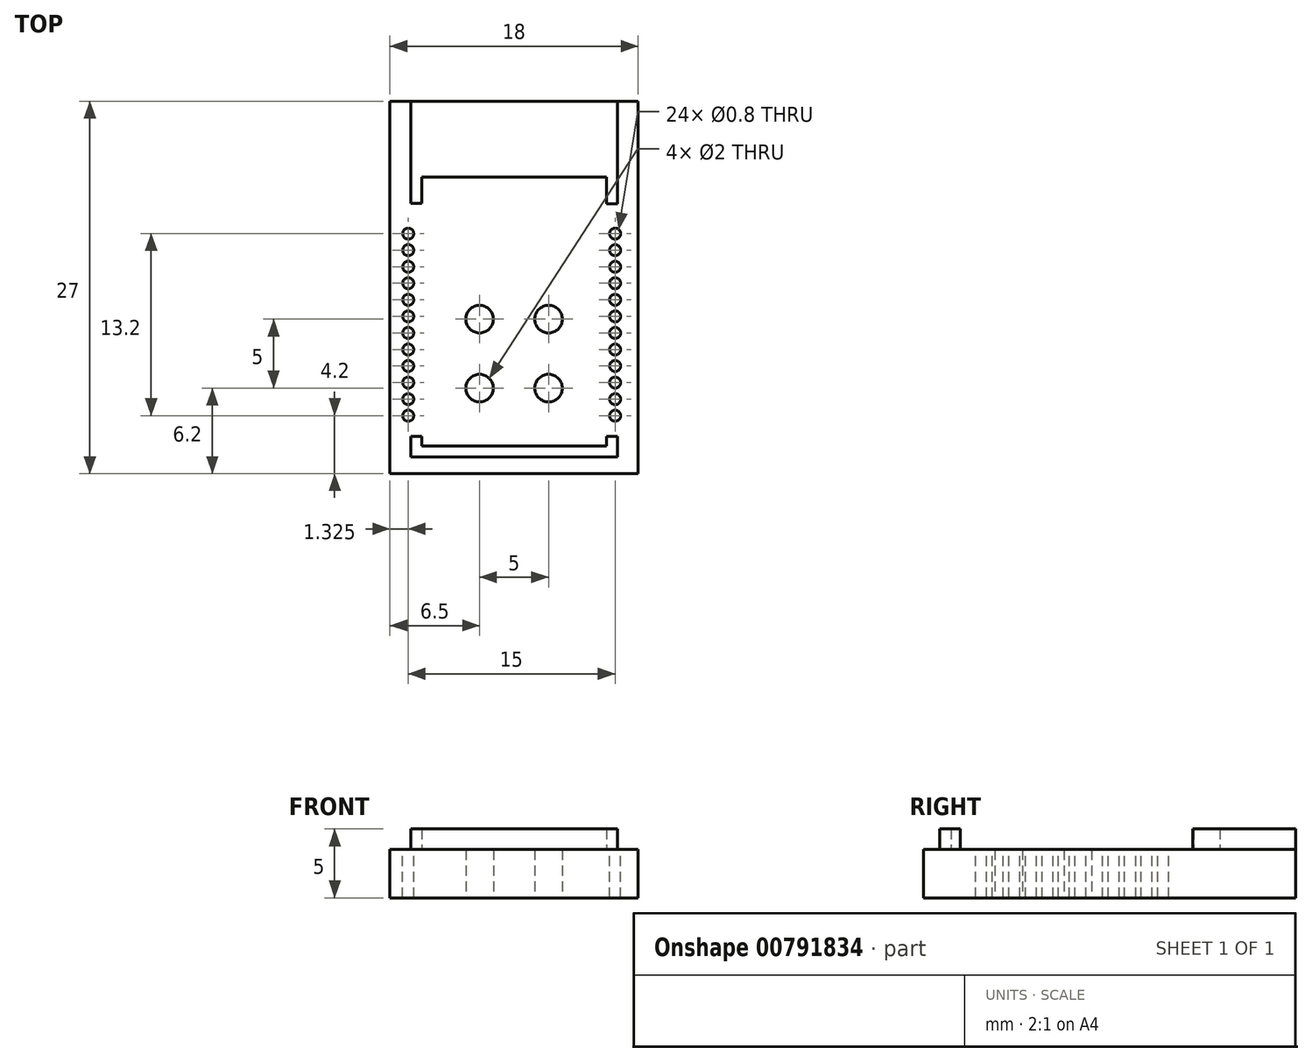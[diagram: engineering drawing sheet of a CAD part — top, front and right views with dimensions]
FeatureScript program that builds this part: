
annotation { "Feature Type Name" : "Feature", "Feature Type Description" : "" }
export const myFeature = defineFeature(function(context is Context, id is Id, definition is map)
    precondition{}
    {
        {
            var Q0;
            Q0=qCreatedBy(makeId("Top.planeOp"),FACE);
            var sketch = newSketch(context, id + "F0", { "sketchPlane" : qUnion([Q0])});
            skLineSegment(sketch, "E0.bottom", {"start": v(0, 0) * mm, "end": v(15, 0) * mm});
            skLineSegment(sketch, "E0.top", {"start": v(0, 25.8) * mm, "end": v(15, 25.8) * mm});
            skLineSegment(sketch, "E0.left", {"start": v(0, 0) * mm, "end": v(0, 1.49) * mm});
            skLineSegment(sketch, "E0.right", {"start": v(15, 0) * mm, "end": v(15, 1.49) * mm});
            skLineSegment(sketch, "E1.bottom", {"start": v(0.8, 0.8) * mm, "end": v(14.2, 0.8) * mm});
            skLineSegment(sketch, "E1.top", {"start": v(0.8, 20.3) * mm, "end": v(14.2, 20.3) * mm});
            skLineSegment(sketch, "E1.left", {"start": v(0.8, 0.8) * mm, "end": v(0.8, 1.49) * mm});
            skLineSegment(sketch, "E1.right", {"start": v(14.2, 0.8) * mm, "end": v(14.2, 1.49) * mm});
            skLineSegment(sketch, "E2.bottom", {"start": v(-1.5, -1.2) * mm, "end": v(16.5, -1.2) * mm});
            skLineSegment(sketch, "E2.top", {"start": v(-1.5, 25.8) * mm, "end": v(16.5, 25.8) * mm});
            skLineSegment(sketch, "E2.left", {"start": v(-1.5, -1.2) * mm, "end": v(-1.5, 25.8) * mm});
            skLineSegment(sketch, "E2.right", {"start": v(16.5, -1.2) * mm, "end": v(16.5, 25.8) * mm});
            skLineSegment(sketch, "E3.bottom", {"start": v(0, 1.49) * mm, "end": v(0.8, 1.49) * mm});
            skLineSegment(sketch, "E3.top", {"start": v(0, 18.4) * mm, "end": v(0.8, 18.4) * mm});
            skLineSegment(sketch, "E4.trimOffspring", {"start": v(0, 18.4) * mm, "end": v(0, 25.8) * mm});
            skLineSegment(sketch, "E5.trimOffspring", {"start": v(0.8, 18.4) * mm, "end": v(0.8, 20.3) * mm});
            skLineSegment(sketch, "E6.bottom", {"start": v(14.2, 1.49) * mm, "end": v(15, 1.49) * mm});
            skLineSegment(sketch, "E6.top", {"start": v(14.2, 18.35) * mm, "end": v(15, 18.35) * mm});
            skLineSegment(sketch, "E7.trimOffspring", {"start": v(14.2, 18.35) * mm, "end": v(14.2, 20.3) * mm});
            skLineSegment(sketch, "E8.trimOffspring", {"start": v(15, 18.35) * mm, "end": v(15, 25.8) * mm});
            skCircle(sketch, "E9", {"center": v(5, 5) * mm, "radius": 1 * mm});
            skCircle(sketch, "E10.0.1.0", {"center": v(5, 10) * mm, "radius": 1 * mm});
            skCircle(sketch, "E10.1.0.0", {"center": v(10, 5) * mm, "radius": 1 * mm});
            skCircle(sketch, "E10.1.1.0", {"center": v(10, 10) * mm, "radius": 1 * mm});
            skLineSegment(sketch, "E10.direction1", {"start": v(5, 5) * mm, "end": v(10, 5) * mm, "construction": true});
            skLineSegment(sketch, "E10.direction2", {"start": v(5, 5) * mm, "end": v(5, 10) * mm, "construction": true});
            skSolve(sketch);
        }
        {
            var Q0;
            Q0=makeQuery(id+"F0.imprint","IMPRINT",FACE,{"disambiguationData":[TD([[makeQuery(id+"F0.imprint","IMPRINT",EDGE,{"derivedFrom":sQuery(id+"F0.wireOp",EDGE,"E0.bottom")}),1.0]])]});
            var Q1;
            Q1=makeQuery(id+"F0.imprint","IMPRINT",FACE,{"disambiguationData":[TD([[makeQuery(id+"F0.imprint","IMPRINT",EDGE,{"derivedFrom":sQuery(id+"F0.wireOp",EDGE,"E1.top")}),1.0]])]});
            extrude(context, id + "F1", {"entities" : qUnion([Q0, Q1]), "depth" : 5 * mm, "offsetDistance" : 25 * mm});
        }
        {
            var Q0;
            Q0=makeQuery(id+"F0.imprint","IMPRINT",FACE,{"disambiguationData":[TD([[makeQuery(id+"F0.imprint","IMPRINT",EDGE,{"derivedFrom":sQuery(id+"F0.wireOp",EDGE,"E1.bottom")}),1.0]])]});
            var Q1;
            {var subQ4=sQuery(id+"F0.wireOp",EDGE,"E0.bottom");Q1=makeQuery(id+"F0.imprint","IMPRINT",FACE,{"disambiguationData":[TD([[makeQuery(id+"F0.imprint","IMPRINT",EDGE,{"derivedFrom":subQ4}),-1.0]])]});}
            extrude(context, id + "F2", {"entities" : qUnion([Q0, Q1]), "operationType" : NewBodyOperationType.ADD, "depth" : 3.5 * mm, "offsetDistance" : 25 * mm});
        }
        {
            var Q0;
            Q0=makeQuery(id+"F2.opExtrude","CAP_FACE",FACE,{"disambiguationData":[OSD([sQuery(id+"F0.wireOp",EDGE,"E1.bottom"),sQuery(id+"F0.wireOp",EDGE,"E1.top"),sQuery(id+"F0.wireOp",EDGE,"E1.left"),sQuery(id+"F0.wireOp",EDGE,"E1.right")])],"isStart":false});
            var sketch = newSketch(context, id + "F3", { "sketchPlane" : qUnion([Q0])});
            skCircle(sketch, "E11", {"center": v(-0.17, 3) * mm, "radius": 0.4 * mm});
            skCircle(sketch, "E12.0.1.0", {"center": v(-0.17, 4.2) * mm, "radius": 0.4 * mm});
            skCircle(sketch, "E12.0.2.0", {"center": v(-0.17, 5.4) * mm, "radius": 0.4 * mm});
            skCircle(sketch, "E12.0.3.0", {"center": v(-0.17, 6.6) * mm, "radius": 0.4 * mm});
            skCircle(sketch, "E12.0.4.0", {"center": v(-0.17, 7.8) * mm, "radius": 0.4 * mm});
            skCircle(sketch, "E12.0.5.0", {"center": v(-0.17, 9) * mm, "radius": 0.4 * mm});
            skCircle(sketch, "E12.0.6.0", {"center": v(-0.17, 10.2) * mm, "radius": 0.4 * mm});
            skCircle(sketch, "E12.0.7.0", {"center": v(-0.17, 11.4) * mm, "radius": 0.4 * mm});
            skCircle(sketch, "E12.0.8.0", {"center": v(-0.17, 12.6) * mm, "radius": 0.4 * mm});
            skCircle(sketch, "E12.0.9.0", {"center": v(-0.17, 13.8) * mm, "radius": 0.4 * mm});
            skCircle(sketch, "E12.0.10.0", {"center": v(-0.17, 15) * mm, "radius": 0.4 * mm});
            skCircle(sketch, "E12.0.11.0", {"center": v(-0.17, 16.2) * mm, "radius": 0.4 * mm});
            skCircle(sketch, "E12.1.0.0", {"center": v(14.82, 3) * mm, "radius": 0.4 * mm});
            skCircle(sketch, "E12.1.1.0", {"center": v(14.82, 4.2) * mm, "radius": 0.4 * mm});
            skCircle(sketch, "E12.1.2.0", {"center": v(14.82, 5.4) * mm, "radius": 0.4 * mm});
            skCircle(sketch, "E12.1.3.0", {"center": v(14.82, 6.6) * mm, "radius": 0.4 * mm});
            skCircle(sketch, "E12.1.4.0", {"center": v(14.82, 7.8) * mm, "radius": 0.4 * mm});
            skCircle(sketch, "E12.1.5.0", {"center": v(14.82, 9) * mm, "radius": 0.4 * mm});
            skCircle(sketch, "E12.1.6.0", {"center": v(14.82, 10.2) * mm, "radius": 0.4 * mm});
            skCircle(sketch, "E12.1.7.0", {"center": v(14.82, 11.4) * mm, "radius": 0.4 * mm});
            skCircle(sketch, "E12.1.8.0", {"center": v(14.82, 12.6) * mm, "radius": 0.4 * mm});
            skCircle(sketch, "E12.1.9.0", {"center": v(14.82, 13.8) * mm, "radius": 0.4 * mm});
            skCircle(sketch, "E12.1.10.0", {"center": v(14.82, 15) * mm, "radius": 0.4 * mm});
            skCircle(sketch, "E12.1.11.0", {"center": v(14.82, 16.2) * mm, "radius": 0.4 * mm});
            skLineSegment(sketch, "E12.direction1", {"start": v(-0.17, 3) * mm, "end": v(14.82, 3) * mm, "construction": true});
            skLineSegment(sketch, "E12.direction2", {"start": v(-0.17, 3) * mm, "end": v(-0.17, 4.2) * mm, "construction": true});
            skSolve(sketch);
        }
        {
            var Q0;
            Q0=qSketchRegion(id+"F3",true);
            extrude(context, id + "F4", {"entities" : qUnion([Q0]), "operationType" : NewBodyOperationType.REMOVE, "endBound" : BoundingType.SYMMETRIC, "oppositeDirection" : true, "depth" : 25 * mm, "offsetDistance" : 25 * mm});
        }
    });
